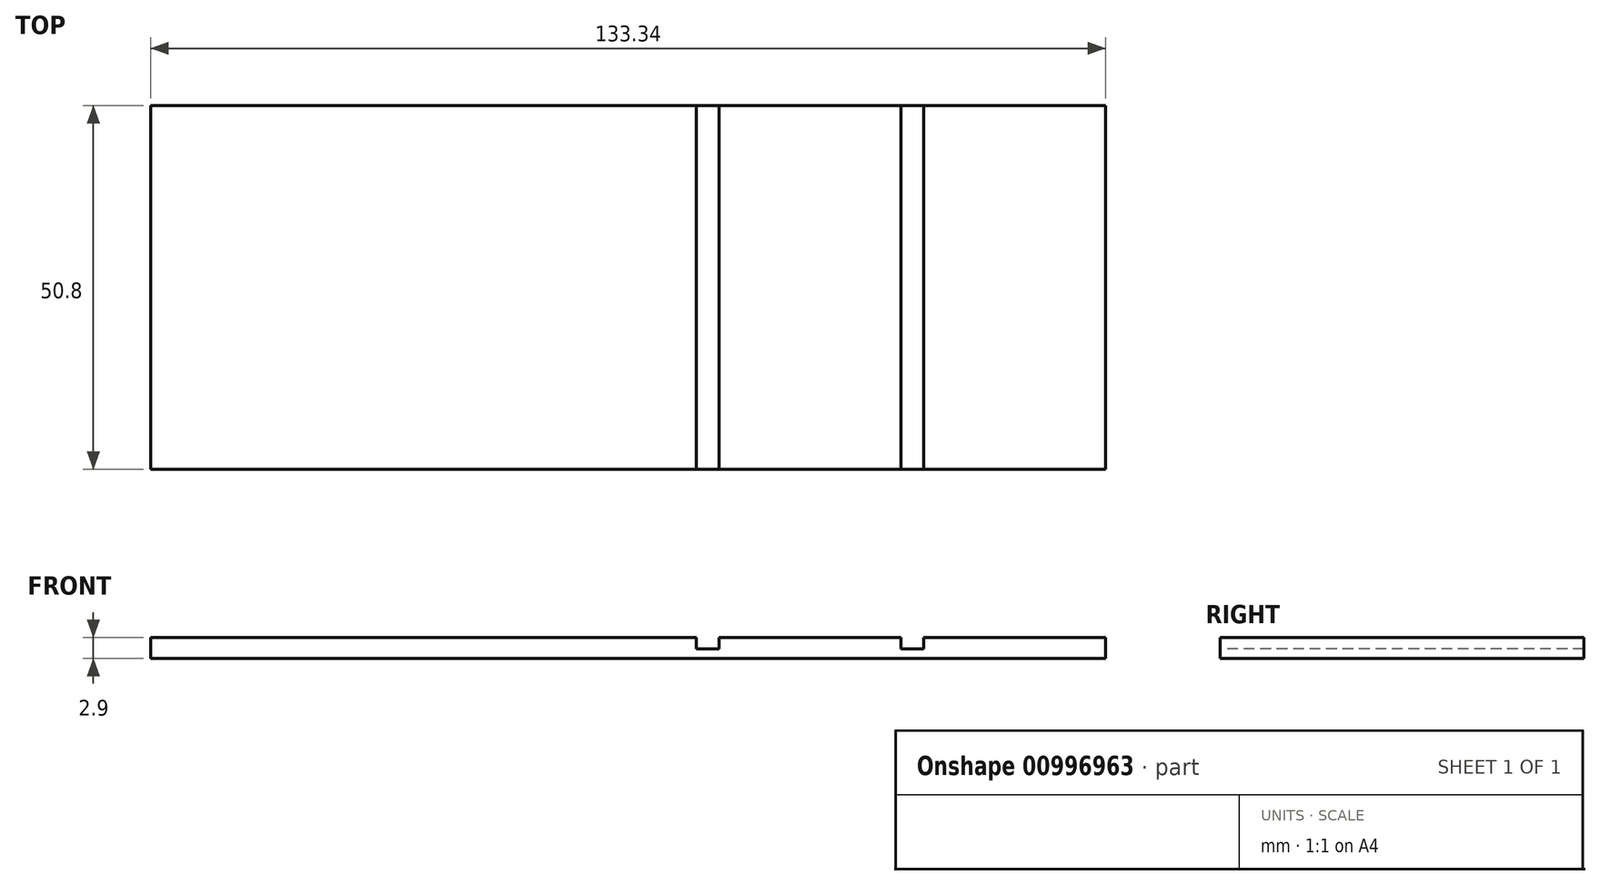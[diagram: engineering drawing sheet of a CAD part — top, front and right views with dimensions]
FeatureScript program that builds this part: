
annotation { "Feature Type Name" : "Feature", "Feature Type Description" : "" }
export const myFeature = defineFeature(function(context is Context, id is Id, definition is map)
    precondition{}
    {
        {
            var Q0;
            Q0=qCreatedBy(makeId("Top.planeOp"),FACE);
            var sketch = newSketch(context, id + "F0", { "sketchPlane" : qUnion([Q0])});
            skLineSegment(sketch, "E0.bottom", {"start": v(66.68, -25.4) * mm, "end": v(-66.67, -25.4) * mm});
            skLineSegment(sketch, "E0.top", {"start": v(66.68, 25.4) * mm, "end": v(-66.68, 25.4) * mm});
            skLineSegment(sketch, "E0.left", {"start": v(66.68, -25.4) * mm, "end": v(66.68, 25.4) * mm});
            skLineSegment(sketch, "E0.right", {"start": v(-66.67, -25.4) * mm, "end": v(-66.68, 25.4) * mm});
            skPoint(sketch, "E0.middle", {"position": v(0, 0) * mm});
            skSolve(sketch);
        }
        {
            var Q0;
            Q0=qSketchRegion(id+"F0",true);
            extrude(context, id + "F1", {"entities" : qUnion([Q0]), "depth" : 2.9 * mm, "offsetDistance" : 25.4 * mm});
        }
        {
            var Q0;
            Q0=makeQuery(id+"F1.opExtrude","CAP_FACE",FACE,{"disambiguationData":[OSD([sQuery(id+"F0.wireOp",EDGE,"E0.bottom"),sQuery(id+"F0.wireOp",EDGE,"E0.top"),sQuery(id+"F0.wireOp",EDGE,"E0.left"),sQuery(id+"F0.wireOp",EDGE,"E0.right")])],"isStart":false});
            var sketch = newSketch(context, id + "F2", { "sketchPlane" : qUnion([Q0])});
            skLineSegment(sketch, "E1.bottom", {"start": v(41.28, 25.4) * mm, "end": v(38.1, 25.4) * mm});
            skLineSegment(sketch, "E1.top", {"start": v(41.28, -25.4) * mm, "end": v(38.1, -25.4) * mm});
            skLineSegment(sketch, "E1.left", {"start": v(41.28, 25.4) * mm, "end": v(41.28, -25.4) * mm});
            skLineSegment(sketch, "E1.right", {"start": v(38.1, 25.4) * mm, "end": v(38.1, -25.4) * mm});
            skLineSegment(sketch, "E2.bottom", {"start": v(9.53, 25.4) * mm, "end": v(12.7, 25.4) * mm});
            skLineSegment(sketch, "E2.top", {"start": v(9.53, -25.4) * mm, "end": v(12.7, -25.4) * mm});
            skLineSegment(sketch, "E2.left", {"start": v(9.53, 25.4) * mm, "end": v(9.53, -25.4) * mm});
            skLineSegment(sketch, "E2.right", {"start": v(12.7, 25.4) * mm, "end": v(12.7, -25.4) * mm});
            skSolve(sketch);
        }
        {
            var Q0;
            Q0=qSketchRegion(id+"F2",true);
            extrude(context, id + "F3", {"entities" : qUnion([Q0]), "operationType" : NewBodyOperationType.REMOVE, "oppositeDirection" : true, "depth" : 1.59 * mm, "offsetDistance" : 25.4 * mm});
        }
    });
